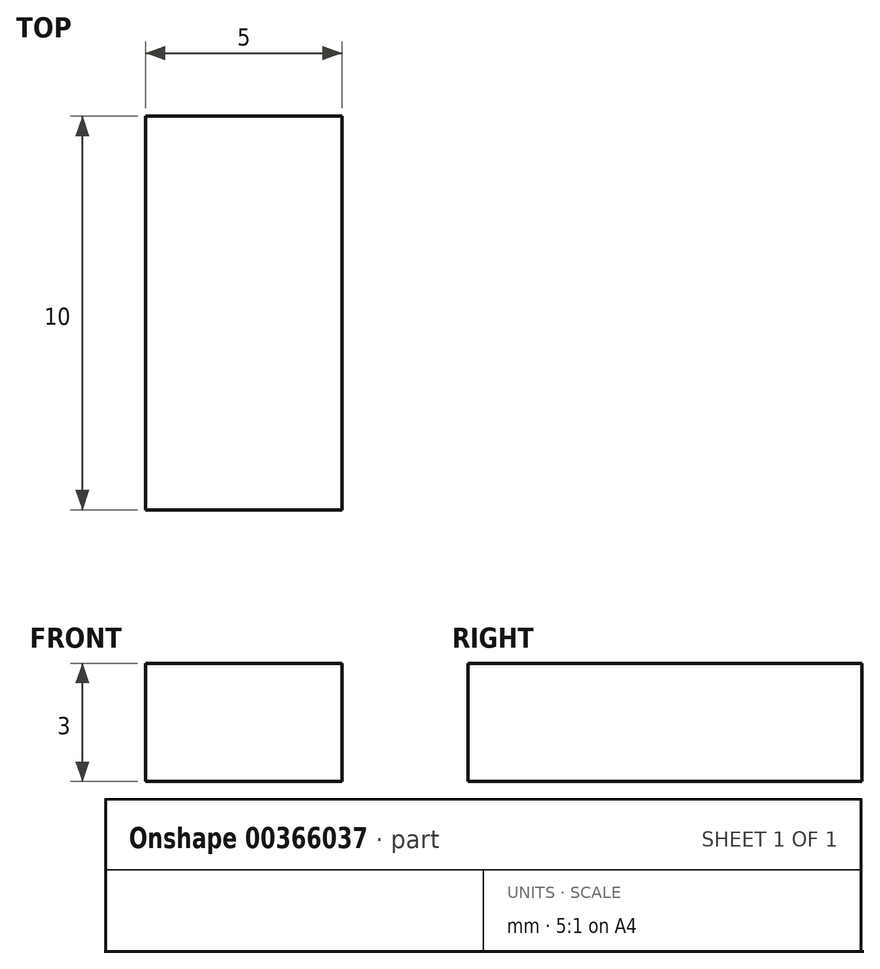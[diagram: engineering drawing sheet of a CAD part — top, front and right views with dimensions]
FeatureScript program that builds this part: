
annotation { "Feature Type Name" : "Feature", "Feature Type Description" : "" }
export const myFeature = defineFeature(function(context is Context, id is Id, definition is map)
    precondition{}
    {
        {
            var Q0;
            Q0=qCreatedBy(makeId("Front.planeOp"),FACE);
            var sketch = newSketch(context, id + "F0", { "sketchPlane" : qUnion([Q0])});
            skLineSegment(sketch, "E0.bottom", {"start": v(0, 0) * mm, "end": v(5, 0) * mm});
            skLineSegment(sketch, "E0.top", {"start": v(0, 3) * mm, "end": v(5, 3) * mm});
            skLineSegment(sketch, "E0.left", {"start": v(0, 0) * mm, "end": v(0, 3) * mm});
            skLineSegment(sketch, "E0.right", {"start": v(5, 0) * mm, "end": v(5, 3) * mm});
            skSolve(sketch);
        }
        {
            var Q0;
            Q0=makeQuery(id+"F0.imprint","IMPRINT",FACE,{"disambiguationData":[TD([[makeQuery(id+"F0.imprint","IMPRINT",EDGE,{"derivedFrom":sQuery(id+"F0.wireOp",EDGE,"E0.bottom")}),1.0]])]});
            extrude(context, id + "F1", {"entities" : qUnion([Q0]), "depth" : 10 * mm});
        }
    });
